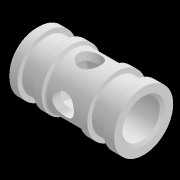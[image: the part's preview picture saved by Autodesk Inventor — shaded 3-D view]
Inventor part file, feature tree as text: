
AUTODESK INVENTOR PART (.ipt)
format: ipt  version: 2021 (Build 250183000, 183)  size: 268,288 bytes
history: native  units: mm
features: sketch x2, revolve x1, chamfer x1, plane x1, hole x1, pattern_circular x1, fillet x1
ambient origin geometry x8: Origin, YZ Plane, XZ Plane, XY Plane, X Axis, Y Axis, Z Axis, Center Point
bodies: Solid1 (feature_tree)
feature tree (8):
  revolve  "Revolution1"  [1 undecoded]
  chamfer  "Chamfer1"  Distance=10.0mm
  plane  "Work Plane1"
  hole  "Hole1"  [1 undecoded]
  pattern_circular  "Circular Pattern1"  [2 undecoded]
  fillet  "Fillet1"  Radius=6.0mm
  sketch  "Sketch2"  dims[d0=7.0mm d1=11.0mm]
  sketch  "Sketch3"  dims[d2=10.0mm d3=10.0mm d5=5.0mm d6=7.5mm d7=6.0mm d8=4.0mm d11=2.0mm d12=3.0mm d13=9.3mm d14=9.3mm d15=3.0mm d16=2.0mm d17=90.0deg d18=0.5mm d19=2.0mm d20=45.0deg d21=4.0mm d22=6.0mm d23=4.0mm d24=2.0mm d25=90.0deg d26=15.0mm d27=20.594885mm d28=40.0mm d29=360.0deg d31=7.0mm d32=0.5mm d33=0.5mm d34=1.15mm d35=1.5mm]
note: 4 required parameter values undecoded (feature->parameter linkage not recoverable at this tier; creation-order binding heuristic only, values carry confidence <= 0.55)